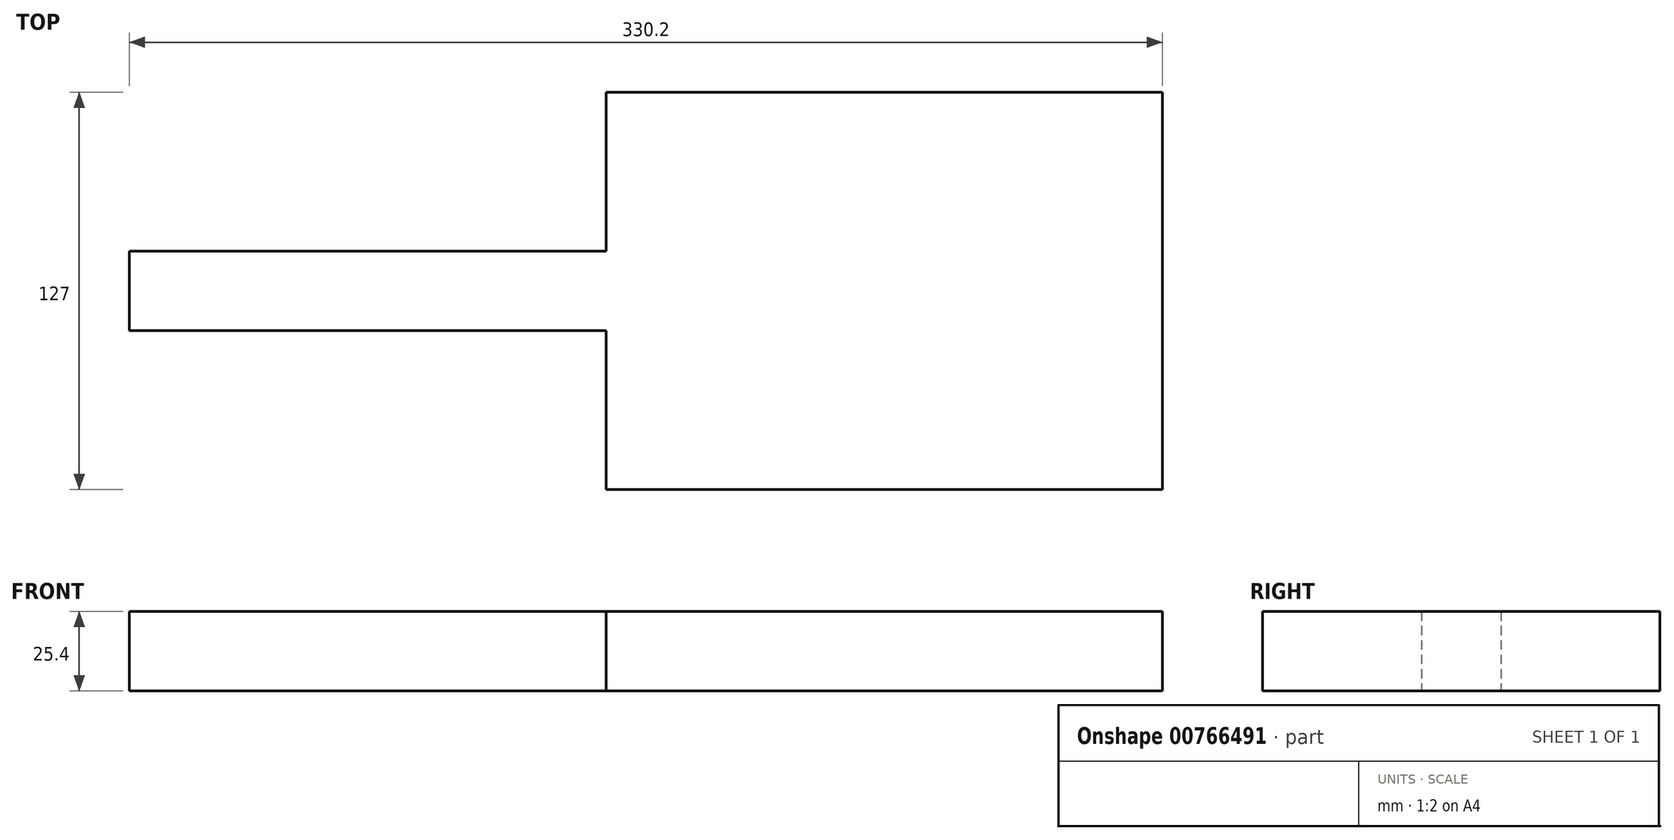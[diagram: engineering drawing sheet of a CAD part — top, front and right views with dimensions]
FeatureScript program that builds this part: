
annotation { "Feature Type Name" : "Feature", "Feature Type Description" : "" }
export const myFeature = defineFeature(function(context is Context, id is Id, definition is map)
    precondition{}
    {
        {
            var Q0;
            Q0=qCreatedBy(makeId("Top.planeOp"),FACE);
            var sketch = newSketch(context, id + "F0", { "sketchPlane" : qUnion([Q0])});
            skLineSegment(sketch, "E0.bottom", {"start": v(0, 0) * mm, "end": v(177.8, 0) * mm});
            skLineSegment(sketch, "E0.top", {"start": v(0, 127) * mm, "end": v(177.8, 127) * mm});
            skLineSegment(sketch, "E0.left", {"start": v(0, 0) * mm, "end": v(0, 127) * mm});
            skLineSegment(sketch, "E0.right", {"start": v(177.8, 0) * mm, "end": v(177.8, 127) * mm});
            skLineSegment(sketch, "E1.bottom", {"start": v(0, 50.8) * mm, "end": v(-152.4, 50.8) * mm});
            skLineSegment(sketch, "E1.top", {"start": v(0, 76.2) * mm, "end": v(-152.4, 76.2) * mm});
            skLineSegment(sketch, "E1.left", {"start": v(0, 50.8) * mm, "end": v(0, 76.2) * mm});
            skLineSegment(sketch, "E1.right", {"start": v(-152.4, 50.8) * mm, "end": v(-152.4, 76.2) * mm});
            skSolve(sketch);
        }
        {
            var Q0;
            Q0=makeQuery(id+"F0.imprint","IMPRINT",FACE,{"disambiguationData":[TD([[makeQuery(id+"F0.imprint","IMPRINT",EDGE,{"derivedFrom":sQuery(id+"F0.wireOp",EDGE,"E1.bottom")}),-1.0]])]});
            var Q1;
            {var subQ3=sQuery(id+"F0.wireOp",EDGE,"E0.bottom");Q1=makeQuery(id+"F0.imprint","IMPRINT",FACE,{"disambiguationData":[TD([[makeQuery(id+"F0.imprint","IMPRINT",EDGE,{"derivedFrom":subQ3}),1.0]])]});}
            extrude(context, id + "F1", {"entities" : qUnion([Q0, Q1]), "depth" : 25.4 * mm, "offsetDistance" : 25.4 * mm});
        }
    });
